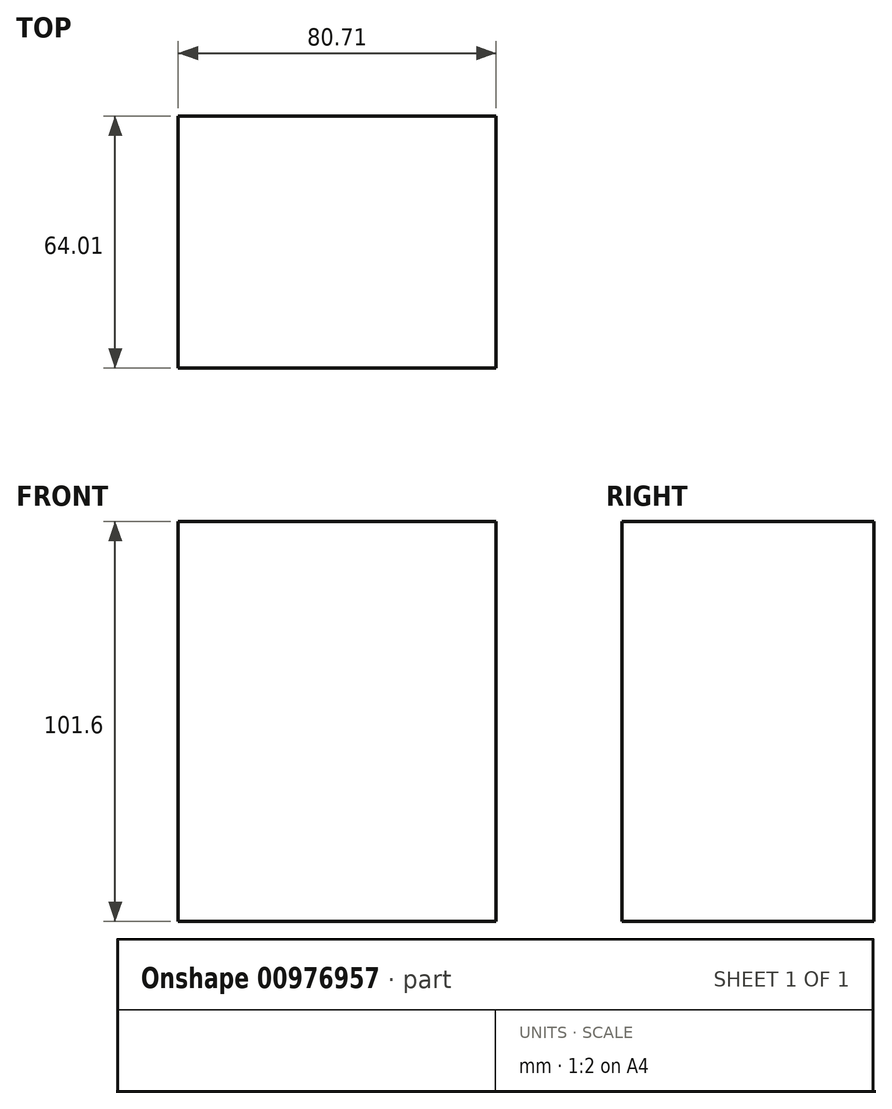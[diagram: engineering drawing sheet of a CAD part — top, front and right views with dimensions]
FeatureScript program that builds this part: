
annotation { "Feature Type Name" : "Feature", "Feature Type Description" : "" }
export const myFeature = defineFeature(function(context is Context, id is Id, definition is map)
    precondition{}
    {
        {
            var Q0;
            Q0=qCreatedBy(makeId("Top.planeOp"),FACE);
            var sketch = newSketch(context, id + "F0", { "sketchPlane" : qUnion([Q0])});
            skLineSegment(sketch, "E0.bottom", {"start": v(26.47, 25.05) * mm, "end": v(-54.24, 25.05) * mm});
            skLineSegment(sketch, "E0.top", {"start": v(26.47, -38.96) * mm, "end": v(-54.24, -38.96) * mm});
            skLineSegment(sketch, "E0.left", {"start": v(26.47, 25.05) * mm, "end": v(26.47, -38.96) * mm});
            skLineSegment(sketch, "E0.right", {"start": v(-54.24, 25.05) * mm, "end": v(-54.24, -38.96) * mm});
            skPoint(sketch, "E0.middle", {"position": v(-13.88, -6.95) * mm});
            skSolve(sketch);
        }
        {
            var Q0;
            Q0=makeQuery(id+"F0.imprint","IMPRINT",FACE,{"disambiguationData":[TD([[makeQuery(id+"F0.imprint","IMPRINT",EDGE,{"derivedFrom":sQuery(id+"F0.wireOp",EDGE,"E0.bottom")}),1.0]])]});
            extrude(context, id + "F1", {"entities" : qUnion([Q0]), "depth" : 101.6 * mm, "offsetDistance" : 25.4 * mm});
        }
    });
